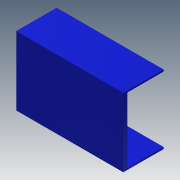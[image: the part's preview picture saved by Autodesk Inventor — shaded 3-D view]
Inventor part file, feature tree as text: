
AUTODESK INVENTOR PART (.ipt)
format: ipt  version: 2013 (Build 170138000, 138)  size: 148,480 bytes
history: native  units: mm
features: extrude x8, sketch x8
ambient origin geometry x8: Origin, YZ Plane, XZ Plane, XY Plane, X Axis, Y Axis, Z Axis, Center Point
bodies: Solid1 (feature_tree)
feature tree (16):
  extrude  "Extrusion1"  Depth=17.0mm
  extrude  "Extrusion2"  Depth=24.7mm
  extrude  "Extrusion3"  Depth=9.0mm TaperAngle=0.0deg
  extrude  "Extrusion4"  Depth=3.0mm
  extrude  "Extrusion5"  Depth=3.0mm
  extrude  "Extrusion6"  Depth=2.0mm TaperAngle=0.0deg
  extrude  "Extrusion7"  Depth=2.0mm
  extrude  "Extrusion8"  Depth=3.0mm
  sketch  "Sketch1"  dims[d0=24.7mm d1=17.0mm]
  sketch  "Sketch2"  dims[d2=10.0mm d3=0.0mm d4=24.7mm]
  sketch  "Sketch3"  dims[d5=16.2mm d6=9.0mm d7=0.0mm]
  sketch  "Sketch4"  dims[d8=3.0mm d9=3.0mm]
  sketch  "Sketch5"  dims[d10=3.0mm d11=3.0mm]
  sketch  "Sketch6"  dims[d12=1.0mm d13=0.0mm d14=2.0mm d15=0.0mm]
  sketch  "Sketch7"  dims[d16=0.2mm d17=0.0mm d18=2.0mm]
  sketch  "Sketch8"  dims[d19=2.0mm d20=3.0mm d21=1.0mm d22=0.0mm d29=3.3mm d30=3.0mm d31=3.0mm d32=1.0mm d33=0.0mm d34=0.1mm d35=0.1mm d36=1.0mm d37=0.0mm]
